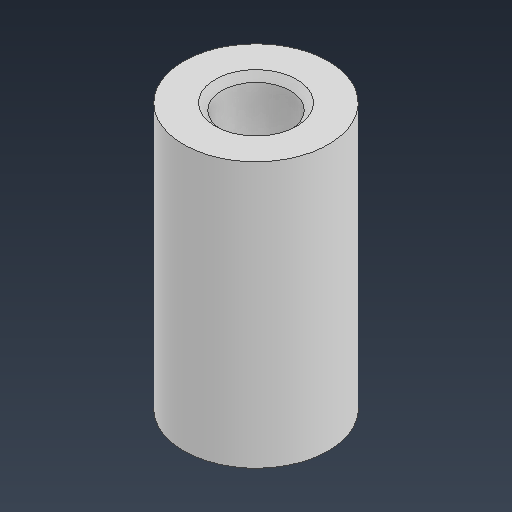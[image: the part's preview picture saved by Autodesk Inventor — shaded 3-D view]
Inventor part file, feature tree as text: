
AUTODESK INVENTOR PART (.ipt)
format: ipt  version: 2025.3 (Build 293356000, 356)  size: 103,936 bytes
history: native  units: mm
features: sketch x3, hole x2, extrude x1
ambient origin geometry x8: Origin, YZ Plane, XZ Plane, XY Plane, X Axis, Y Axis, Z Axis, Center Point
bodies: Solid1 (feature_tree)
feature tree (6):
  extrude  "Extrusion1"  Depth=14.68mm TaperAngle=0.0deg
  sketch  "Sketch2"  dims[d3=3.78mm d4=6.0mm d5=4.5mm d6=2.0mm d7=90.0deg d8=6.0mm d9=0.0mm]
  hole  "Hole1"  [1 undecoded]
  hole  "Hole2"  [1 undecoded]
  sketch  "Sketch1"  dims[d0=8.0mm d1=14.68mm d2=0.0mm]
  sketch  "Sketch3"  dims[d10=3.78mm d11=6.0mm d12=4.5mm d13=2.0mm d14=90.0deg d15=6.0mm d16=0.0mm]
note: 2 required parameter values undecoded (feature->parameter linkage not recoverable at this tier; creation-order binding heuristic only, values carry confidence <= 0.55)
